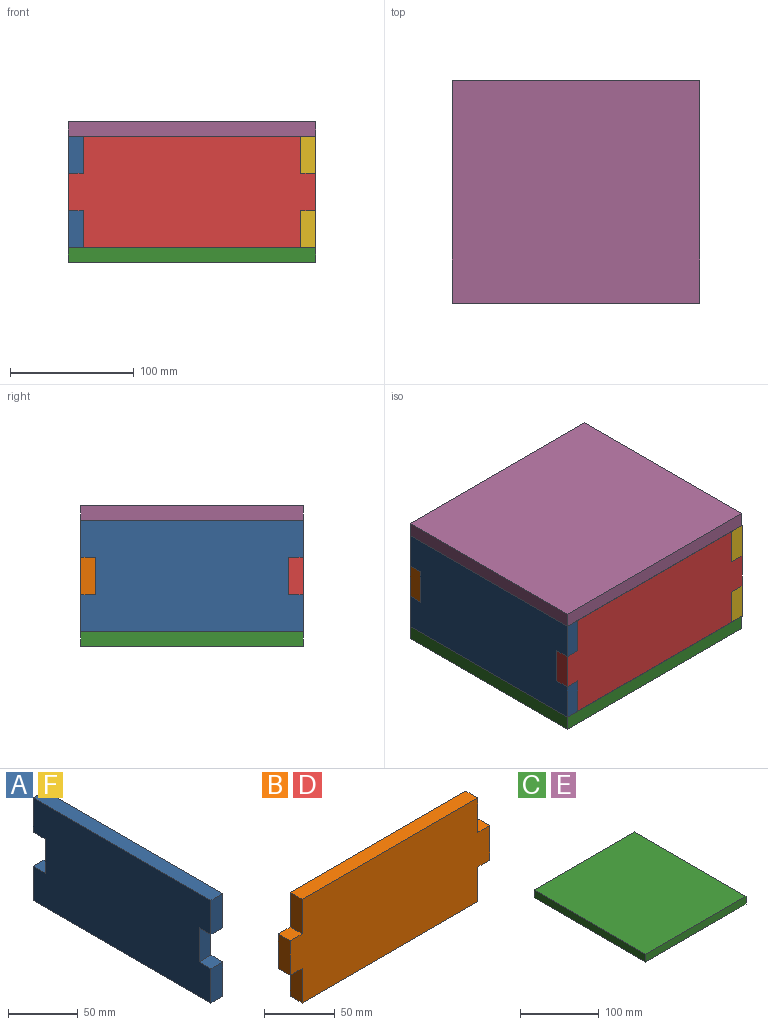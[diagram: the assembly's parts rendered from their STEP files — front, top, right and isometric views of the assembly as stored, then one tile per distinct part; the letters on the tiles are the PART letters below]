
ASSEMBLY  parts=6 mates=5
PART A: 14 faces, bbox 12x180x90 mm
  f0: plane 30x12mm, normal (0,1,0), area 360mm2, adj f1,f11,f12,f13
  f1: plane 12x12mm, normal (0,0,-1), area 144mm2, adj f0,f2,f12,f13
  f2: plane 30x12mm, normal (0,1,0), area 360mm2, adj f1,f3,f12,f13
  f3: plane 180x12mm, normal (0,0,1), area 2160mm2, adj f2,f4,f12,f13
  f4: plane 30x12mm, normal (0,-1,0), area 360mm2, adj f3,f5,f12,f13
  f5: plane 12x12mm, normal (0,0,-1), area 144mm2, adj f4,f6,f12,f13
  f6: plane 30x12mm, normal (0,-1,0), area 360mm2, adj f5,f7,f12,f13
  f7: plane 12x12mm, normal (0,0,1), area 144mm2, adj f6,f8,f12,f13
  f8: plane 30x12mm, normal (0,-1,0), area 360mm2, adj f7,f9,f12,f13
  f9: plane 180x12mm, normal (0,0,-1), area 2160mm2, adj f8,f10,f12,f13
  f10: plane 30x12mm, normal (0,1,0), area 360mm2, adj f9,f11,f12,f13
  f11: plane 12x12mm, normal (0,0,1), area 144mm2, adj f0,f10,f12,f13
  f12: plane 180x90mm, normal (1,0,0), area 15480mm2, adj f0,f1,f2,f3,f4,f5,f6,f7
  f13: plane 180x90mm, normal (-1,0,0), area 15480mm2, adj f0,f1,f2,f3,f4,f5,f6,f7
PART B: 14 faces, bbox 200x12x90 mm
  f0: plane 30x12mm, normal (-1,0,0), area 360mm2, adj f1,f11,f12,f13
  f1: plane 12x12mm, normal (0,0,-1), area 144mm2, adj f0,f2,f12,f13
  f2: plane 30x12mm, normal (-1,0,0), area 360mm2, adj f1,f3,f12,f13
  f3: plane 176x12mm, normal (0,0,-1), area 2112mm2, adj f2,f4,f12,f13
  f4: plane 30x12mm, normal (1,0,0), area 360mm2, adj f3,f5,f12,f13
  f5: plane 12x12mm, normal (0,0,-1), area 144mm2, adj f4,f6,f12,f13
  f6: plane 30x12mm, normal (1,0,0), area 360mm2, adj f5,f7,f12,f13
  f7: plane 12x12mm, normal (0,0,1), area 144mm2, adj f6,f8,f12,f13
  f8: plane 30x12mm, normal (1,0,0), area 360mm2, adj f7,f9,f12,f13
  f9: plane 176x12mm, normal (0,0,1), area 2112mm2, adj f8,f10,f12,f13
  f10: plane 30x12mm, normal (-1,0,0), area 360mm2, adj f9,f11,f12,f13
  f11: plane 12x12mm, normal (0,0,1), area 144mm2, adj f0,f10,f12,f13
  f12: plane 200x90mm, normal (0,-1,0), area 16560mm2, adj f0,f1,f2,f3,f4,f5,f6,f7
  f13: plane 200x90mm, normal (0,1,0), area 16560mm2, adj f0,f1,f2,f3,f4,f5,f6,f7
PART C: 6 faces, bbox 180x200x12 mm
  f0: plane 180x12mm, normal (0,1,0), area 2160mm2, adj f1,f3,f4,f5
  f1: plane 200x12mm, normal (-1,0,0), area 2400mm2, adj f0,f2,f4,f5
  f2: plane 180x12mm, normal (0,-1,0), area 2160mm2, adj f1,f3,f4,f5
  f3: plane 200x12mm, normal (1,0,0), area 2400mm2, adj f0,f2,f4,f5
  f4: plane 200x180mm, normal (0,0,1), area 36000mm2, adj f0,f1,f2,f3
  f5: plane 200x180mm, normal (0,0,-1), area 36000mm2, adj f0,f1,f2,f3
PART D: same geometry as B
PART E: same geometry as C
PART F: same geometry as A
PLACE A t=(-279.53,-81.42,47.14)mm
PLACE B t=(-97.53,92.58,47.14)mm
PLACE C rot(axis=(0,0,-1),90deg) t=(-285.53,98.58,41.14)mm
PLACE D t=(-97.53,-75.42,47.14)mm
PLACE E rot(axis=(0,0,-1),90deg) t=(-285.53,98.58,143.14)mm
PLACE F t=(-91.53,-81.42,47.14)mm fixed
MATE fastened D.f7 <-> F.f5  axis (0,0,1) through (-85.53,-69.42,107.14)mm
MATE fastened D.f11 <-> A.f5  axis (0,0,1) through (-285.53,-69.42,107.14)mm
MATE fastened B.f7 <-> F.f1  axis (0,0,1) through (-85.53,86.58,107.14)mm
MATE fastened A.f3 <-> E.f5  axis (0,0,1) through (-285.53,-81.42,137.14)mm
MATE fastened A.f9 <-> C.f4  axis (0,0,1) through (-285.53,98.58,47.14)mm
